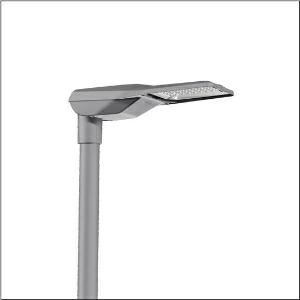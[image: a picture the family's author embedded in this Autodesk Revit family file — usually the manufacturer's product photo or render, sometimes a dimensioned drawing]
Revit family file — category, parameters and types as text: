
# Revit family: streetlight_sl_21_iq_mini___pl52_5xe2h31g08hb_1606
name_source: partatom
category: Lighting Fixtures
units: mm (PartAtom-declared; Revit-internal decimal feet)

## family parameters
Cut with Voids When Loaded = No
Host = Face
Light Source = No
Part Type = Normal
Room Calculation Point = No
Round Connector Dimension = Use Diameter
Shared = No

## types (1)
- --- (1 x LED, 9290 lm, 70.9 W, 3000K)
    Apparent Load = 71 VA
    CIE Flux Codes = 27 59 98 100 100
    Color Rendering = 70
    Color Temperature = 3000K
    Default Elevation = 1800 mm
    Description = Streetlight SL 21 iQ mini, mast luminaire, primary light control with lens, of PMMA, primary optical cover: cover, of toughened safety glass, transparent, light distribution: PL52, light emission: direct distribution, primary light characteristic: asymmetric, installation type: post-top, side-entry, LED, High Power LED, rated luminous flux: 9.290lm, luminous efficacy: 131lm/W, light colour: 730, colour temperature: 3000K, control: Street-Remote, Auto-Match, Temp-Guard, Lumen-Switch, Night-Set, Smart-Wire, Light-Fading, Desk-Remote (wireless, voltage-free reading and setting of iQ features in the workshop via application-optimized NFC function/RFID function), optimised constant luminous flux control (CLO 2.0), presetting dimming linear, mains connection: 220..240V, AC, 50/60Hz, start of lifetime: 71W, end of service life: 75W, reduction: 31W, luminaire housing, of diecast aluminium, powder-coated, Siteco® metallic grey (DB 702S), corrosivity category C5 mid according to DIN EN ISO 12944, please order mast flange separately, inclination adjustable: 0°, 5°, 10°, 15°, sealing non-destructively replaceable, multi-level sealing system, length: 628mm, width: 235mm, height: 110mm, mast flange for spigot size: 42mm (side-entry): 5XC10008XM4, 60/48mm (side-entry/post-top): 5XC10108XM2, 76/60mm (side-entry/post-top): 5XC10108XM1, protection rating (complete): IP66, insulation class (complete): insulation class II (safety insulation), certification: CE, ENEC, ENEC+, VDE, impact resistance: IK09, permissible operating ambient temperature for outdoor applications: -40..+50°C, standard-compliant lighting for roads and squares, packaging unit: 1 piece

Light Distribution: PL52
    Height = 110 mm
    Lamp = 1 x LED
    Lamp Light Flux = 9290 lm
    Lamp Power = 70.9 W
    Lamp count = 1
    Length = 625 mm
    Luminous efficacy = 131 lm/W
    Manufacturer = Siteco
    ModVariant = No
    Model = 5XE2H31G08HB
    Number of Poles = 1
    OnlyDefault = Yes
    Power Factor = 1
    Product Name = Streetlight SL 21 iQ mini | PL52
    Product group = mast luminaire | pylon top
    ProductGroupID = 6100
    Protection Class = Protection class II
    Protection Degree = IP 66
    RLX_Detail_Level = 1
    RLX_Emergency_Light_Flux = 0 lm
    RLX_Emergency_Type = 0
    RLX_Emergency_Type_DB = No
    RlxData = <blob elided: 101845 chars, md5=540ce336>
    Socket = socket
    Standby Power = 0 W
    System Light Flux = 9290 lm
    System Power = 71 W
    Type Comments = factory setting: luminous flux: 100 % | dim-lin: 254 | 711 mA
    Type Image = l_1003519.jpg
    URL = http://relux.com
    VarID = @adj_090761
    Voltage = 0 V
    Weight = 0.00 kg
    Width = 234 mm

## geometry (parser evidence)
native form markers: Blend x4, Sweep x12
no freeform markers — native parametric forms only
